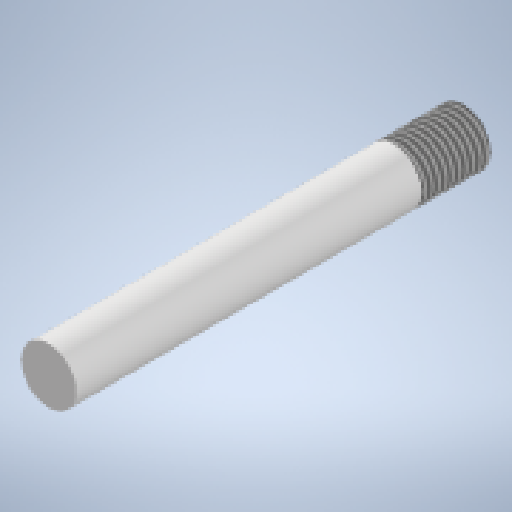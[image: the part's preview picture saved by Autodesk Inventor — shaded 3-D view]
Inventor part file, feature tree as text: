
AUTODESK INVENTOR PART (.ipt)
format: ipt  version: 2023 (Build 270158000, 158)  size: 140,800 bytes
history: native  units: mm
features: extrude x1, thread x1, sketch x1
ambient origin geometry x8: Origin, YZ Plane, XZ Plane, XY Plane, X Axis, Y Axis, Z Axis, Center Point
bodies: Solid1 (feature_tree)
feature tree (3):
  extrude  "Extrusion1"  Depth=30.0mm TaperAngle=0.0deg
  thread  "Thread1"  [1 undecoded]
  sketch  "Sketch1"  dims[d0=4.0mm d1=30.0mm d2=0.0mm d3=5.0mm d4=0.0mm]
note: 1 required parameter value undecoded (feature->parameter linkage not recoverable at this tier; creation-order binding heuristic only, values carry confidence <= 0.55)
